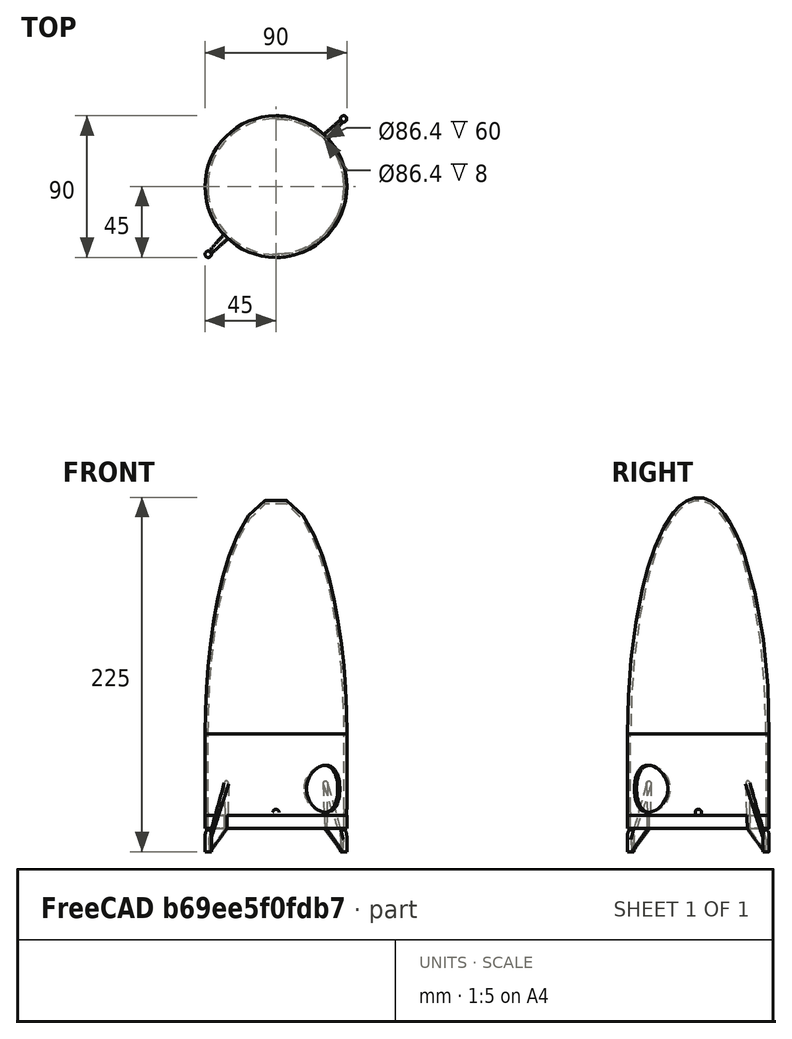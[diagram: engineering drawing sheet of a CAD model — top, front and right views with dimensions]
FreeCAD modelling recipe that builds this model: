
FCSTD DOCUMENT  (FreeCAD 1.0R39109 (Git))
Label: 251_etage2b_coiffe
License: All rights reserved
LicenseURL: https://en.wikipedia.org/wiki/All_rights_reserved
objects: Part::Ellipsoid×4, Sketcher::SketchObject×4, Part::Cylinder×3, PartDesign::FeatureBase×3, PartDesign::Body×3, Part::Fuse×3, Part::FeaturePython×2, Part::Cut×2, PartDesign::Pocket×2, PartDesign::PolarPattern×2, PartDesign::AdditiveLoft×1, App::Part×1
note: 44 computed .brp shape members not serialized (recipe doc carries the construction recipe); baked Part::Feature solids carry a one-line shape summary decoded from their .brp

FEATURE [Part::FeaturePython] Tube  label="Tube corps"  # WARN: FeaturePython — macro-defined, semantics opaque (R4)
  AttacherType = Attacher::AttachEngine3D
  Height = 60
  InnerRadius = 43.2
  OuterRadius = 45
FEATURE [Part::Ellipsoid] Ellipsoid002  label="Coiffe exterieure"
  Angle1 = -90
  Angle2 = 90
  Angle3 = 360
  AttacherType = Attacher::AttachEngine3D
  Placement = pos=(0,0,50) rot=(1,0,0;1.5708rad)
  Radius1 = 45
  Radius2 = 45
  Radius3 = 150
FEATURE [Part::Cylinder] Cylinder  label="Suppression moitié ellipse"
  Angle = 360
  AttacherType = Attacher::AttachEngine3D
  FirstAngle = 0
  Height = 150
  Placement = pos=(0,0,-100) rot=(0,0,1;0rad)
  Radius = 45
  SecondAngle = 0
FEATURE [Part::Cut] Cut
  Base = -> Ellipsoid002
  Tool = -> Cylinder
FEATURE [Part::Ellipsoid] Ellipsoid  label="Creux de la coiffe"
  Angle1 = -90
  Angle2 = 90
  Angle3 = 360
  AttacherType = Attacher::AttachEngine3D
  Placement = pos=(0,0,50) rot=(1,0,0;1.5708rad)
  Radius1 = 43
  Radius2 = 43
  Radius3 = 148
FEATURE [Part::Cut] Cut001  label="Coiffe"
  Base = -> Cut
  Placement = pos=(0,0,10) rot=(0,0,1;0rad)
  Tool = -> Ellipsoid
FEATURE [Sketcher::SketchObject] Sketch
  ArcFitTolerance = 0
  AttachmentSupport = -> [XZ_Plane001]
  FullyConstrained = true
  MakeInternals = false
  MapMode = 5
  Placement = pos=(0,0,0) rot=(1,0,0;1.5708rad)
  sketch-geometry (1):
    g0: Circle CenterX=0 CenterY=10 CenterZ=0 NormalX=0 NormalY=0 NormalZ=1 AngleXU=0 Radius=2
  constraints (3):
    c: DistanceY(g-1,g0) = 10
    c: DistanceX(g-1,g0) = 0
    c: Radius(g0) = 2
FEATURE [PartDesign::FeatureBase] BaseFeature
  BaseFeature = -> Tube
  Suppressed = false
FEATURE [PartDesign::Pocket] Pocket
  BaseFeature = -> BaseFeature
  Direction = (0,1,2e-16)
  Length = 5
  Length2 = 5
  Midplane = true
  Profile = -> Sketch
  ReferenceAxis = -> Sketch [N_Axis]
  Suppressed = false
  Type = 1
FEATURE [PartDesign::PolarPattern] PolarPattern
  Angle = 360
  Axis = -> Sketch [V_Axis]
  BaseFeature = -> Pocket
  Mode = 0
  Occurrences = 4
  Offset = 120
  Originals = -> [Pocket]
  Suppressed = false
  TransformMode = 0
FEATURE [Sketcher::SketchObject] Sketch001
  ArcFitTolerance = 0
  AttachmentOffset = pos=(0,0,44.5) rot=(0,1,0;0rad)
  AttachmentSupport = -> [YZ_Plane002]
  FullyConstrained = true
  MakeInternals = false
  MapMode = 5
  Placement = pos=(44.5,0,0) rot=(0.57735,0.57735,0.57735;2.0944rad)
  sketch-geometry (4):
    g0: ArcOfCircle CenterX=0 CenterY=28 CenterZ=0 NormalX=0 NormalY=0 NormalZ=1 AngleXU=0 Radius=2 StartAngle=0 EndAngle=3.14159
    g1: LineSegment StartX=-1 StartY=0 StartZ=0 EndX=1 EndY=0 EndZ=0
    g2: LineSegment StartX=-2 StartY=28 StartZ=0 EndX=-1 EndY=0 EndZ=0
    g3: LineSegment StartX=2 StartY=28 StartZ=0 EndX=1 EndY=0 EndZ=0
  constraints (13):
    c: PointOnObject(g0,g-2)
    c: Horizontal(g0,g0)
    c: Horizontal(g0,g0)
    c: Radius(g0) = 2
    c: DistanceY(g-1,g0) = 28
    c: PointOnObject(g1,g-1)
    c: PointOnObject(g1,g-1)
    c: DistanceX(g-1,g1) = 1
    c: DistanceX(g1,g-1) = 1
    c: Coincident(g2,g0)
    c: Coincident(g2,g1)
    c: Coincident(g3,g0)
    c: Coincident(g3,g1)
FEATURE [Sketcher::SketchObject] Sketch002
  ArcFitTolerance = 0
  AttachmentOffset = pos=(0,0,59.5) rot=(0,0,1;0rad)
  AttachmentSupport = -> [YZ_Plane002]
  FullyConstrained = true
  MakeInternals = false
  MapMode = 5
  Placement = pos=(59.5,0,0) rot=(0.57735,0.57735,0.57735;2.0944rad)
  sketch-geometry (4):
    g0: ArcOfCircle CenterX=0 CenterY=-7 CenterZ=0 NormalX=0 NormalY=0 NormalZ=1 AngleXU=0 Radius=1 StartAngle=0 EndAngle=3.14159
    g1: LineSegment StartX=-0.5 StartY=-15 StartZ=0 EndX=0.5 EndY=-15 EndZ=0
    g2: LineSegment StartX=1 StartY=-7 StartZ=0 EndX=0.5 EndY=-15 EndZ=0
    g3: LineSegment StartX=-1 StartY=-7 StartZ=0 EndX=-0.5 EndY=-15 EndZ=0
  constraints (13):
    c: PointOnObject(g0,g-2)
    c: Radius(g0) = 1
    c: Horizontal(g0,g0)
    c: DistanceX(g1,g-1) = 0.5
    c: DistanceX(g-1,g1) = 0.5
    c: Horizontal(g1,g1)
    c: Coincident(g2,g0)
    c: Coincident(g2,g1)
    c: Coincident(g3,g0)
    c: Coincident(g3,g1)
    c: Distance(g0,g1) = 8
    c: Horizontal(g0,g0)
    c: DistanceY(g1,g-1) = 15
FEATURE [Part::FeaturePython] Tube001  label="Tube porte ailerons"  # WARN: FeaturePython — macro-defined, semantics opaque (R4)
  AttacherType = Attacher::AttachEngine3D
  Height = 8
  InnerRadius = 43.2
  OuterRadius = 45
FEATURE [PartDesign::FeatureBase] BaseFeature001
  BaseFeature = -> Tube001
  Suppressed = false
FEATURE [PartDesign::AdditiveLoft] AdditiveLoft
  BaseFeature = -> BaseFeature001
  Closed = false
  Profile = -> Sketch001
  Ruled = false
  Sections = -> [Sketch002]
  Suppressed = false
FEATURE [Sketcher::SketchObject] Sketch003
  ArcFitTolerance = 0
  AttachmentOffset = pos=(0,0,0) rot=(0,1,0;2.35619rad)
  AttachmentSupport = -> [YZ_Plane001]
  FullyConstrained = true
  MakeInternals = false
  MapMode = 5
  Placement = pos=(0,0,0) rot=(-0.281085,0.678598,0.678598;3.68962rad)
  sketch-geometry (1):
    g0: Circle CenterX=0 CenterY=25 CenterZ=0 NormalX=0 NormalY=0 NormalZ=1 AngleXU=0 Radius=15
  constraints (3):
    c: PointOnObject(g0,g-2)
    c: Radius(g0) = 15
    c: DistanceY(g-1,g0) = 25
FEATURE [PartDesign::Pocket] Pocket001
  BaseFeature = -> PolarPattern
  Direction = (0.707107,-0.707107,3e-16)
  Length = 5
  Length2 = 5
  Profile = -> Sketch003
  ReferenceAxis = -> Sketch003 [N_Axis]
  Suppressed = false
  Type = 1
FEATURE [PartDesign::Body] Body  label="Corps"
  AllowCompound = false
  BaseFeature = -> Tube
  Group = -> [BaseFeature,Sketch,Pocket,PolarPattern,Sketch003,Pocket001]
  Origin = -> Origin001
  Tip = -> Pocket001
FEATURE [Part::Cylinder] Cylinder001  label="Cylindre"
  Angle = 360
  AttacherType = Attacher::AttachEngine3D
  FirstAngle = 0
  Height = 10
  Placement = pos=(43,43,-15) rot=(0,0,1;0.785398rad)
  Radius = 2
  SecondAngle = 0
FEATURE [Part::Ellipsoid] Ellipsoid003  label="Ellipsoïde"
  Angle1 = -90
  Angle2 = 90
  Angle3 = 360
  AttacherType = Attacher::AttachEngine3D
  Placement = pos=(43,43,-5) rot=(0,0,1;0rad)
  Radius1 = 4
  Radius2 = 2
  Radius3 = 2
FEATURE [PartDesign::PolarPattern] PolarPattern001
  Angle = 360
  Axis = -> Z_Axis002
  BaseFeature = -> AdditiveLoft
  Mode = 0
  Occurrences = 2
  Offset = 120
  Originals = -> [AdditiveLoft]
  Suppressed = false
  TransformMode = 0
FEATURE [PartDesign::Body] Body001  label="Ailerons"
  AllowCompound = false
  BaseFeature = -> Tube001
  Group = -> [BaseFeature001,Sketch001,Sketch002,AdditiveLoft,PolarPattern001]
  Origin = -> Origin002
  Placement = pos=(0,0,0) rot=(0,0,1;0.785398rad)
  Tip = -> PolarPattern001
FEATURE [Part::Cylinder] Cylinder002  label="Cylindre001"
  Angle = 360
  AttacherType = Attacher::AttachEngine3D
  FirstAngle = 0
  Height = 10
  Placement = pos=(-43,-43,-15) rot=(0,0,1;0.785398rad)
  Radius = 2
  SecondAngle = 0
FEATURE [Part::Ellipsoid] Ellipsoid004  label="Ellipsoïde001"
  Angle1 = -90
  Angle2 = 90
  Angle3 = 360
  AttacherType = Attacher::AttachEngine3D
  Placement = pos=(-43,-43,-5) rot=(0,0,1;0rad)
  Radius1 = 4
  Radius2 = 2
  Radius3 = 2
FEATURE [Part::Fuse] Fusion
  Base = -> Cylinder001
  Tool = -> Ellipsoid003
FEATURE [Part::Fuse] Fusion001
  Base = -> Cylinder002
  Tool = -> Ellipsoid004
FEATURE [Part::Fuse] Fusion002
  Base = -> Fusion
  Tool = -> Fusion001
FEATURE [PartDesign::FeatureBase] BaseFeature002
  BaseFeature = -> Fusion002
  Suppressed = false
FEATURE [PartDesign::Body] Body002  label="Corps001"
  AllowCompound = false
  BaseFeature = -> Fusion002
  Group = -> [BaseFeature002]
  Origin = -> Origin003
  Tip = -> BaseFeature002
FEATURE [App::Part] Part
  Group = -> [Ellipsoid002,Ellipsoid,Cut,Cylinder,Cut001,Body,Body001,Ellipsoid003,Ellipsoid004,Cylinder001,Cylinder002,Fusion001,Fusion,Fusion002,Body002,Tube,Tube001]
  Origin = -> Origin
